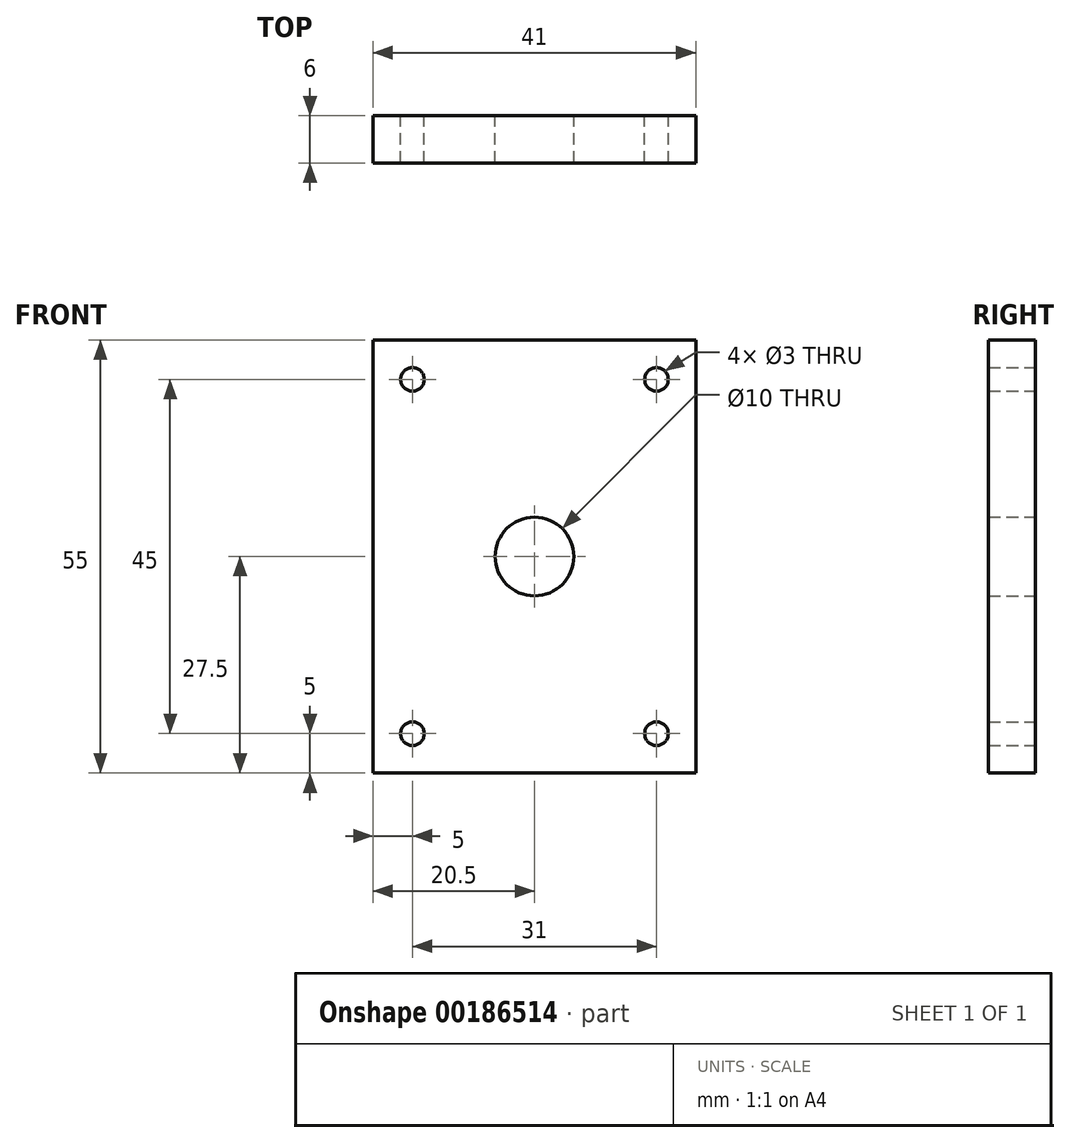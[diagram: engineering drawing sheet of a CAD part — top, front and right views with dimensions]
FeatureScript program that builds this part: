
annotation { "Feature Type Name" : "Feature", "Feature Type Description" : "" }
export const myFeature = defineFeature(function(context is Context, id is Id, definition is map)
    precondition{}
    {
        {
            var Q0;
            Q0=qCreatedBy(makeId("Front.planeOp"),FACE);
            var sketch = newSketch(context, id + "F0", { "sketchPlane" : qUnion([Q0])});
            skLineSegment(sketch, "E0.bottom", {"start": v(-20.5, -27.5) * mm, "end": v(20.5, -27.5) * mm});
            skLineSegment(sketch, "E0.top", {"start": v(-20.5, 27.5) * mm, "end": v(20.5, 27.5) * mm});
            skLineSegment(sketch, "E0.left", {"start": v(-20.5, -27.5) * mm, "end": v(-20.5, 27.5) * mm});
            skLineSegment(sketch, "E0.right", {"start": v(20.5, -27.5) * mm, "end": v(20.5, 27.5) * mm});
            skPoint(sketch, "E0.middle", {"position": v(0, 0) * mm});
            skCircle(sketch, "E1", {"center": v(-15.5, 22.5) * mm, "radius": 1.5 * mm});
            skLineSegment(sketch, "E2", {"start": v(-20.5, 0) * mm, "end": v(20.5, 0) * mm, "construction": true});
            skLineSegment(sketch, "E3", {"start": v(0, 27.5) * mm, "end": v(0, -27.5) * mm, "construction": true});
            skCircle(sketch, "E4.MirrorC", {"center": v(15.5, 22.5) * mm, "radius": 1.5 * mm});
            skCircle(sketch, "E5.MirrorC", {"center": v(-15.5, -22.5) * mm, "radius": 1.5 * mm});
            skCircle(sketch, "E6.MirrorC", {"center": v(15.5, -22.5) * mm, "radius": 1.5 * mm});
            skCircle(sketch, "E7", {"center": v(0, 0) * mm, "radius": 5 * mm});
            skSolve(sketch);
        }
        {
            var Q0;
            Q0=qSketchRegion(id+"F0",true);
            extrude(context, id + "F1", {"entities" : qUnion([Q0]), "depth" : 6 * mm});
        }
    });
